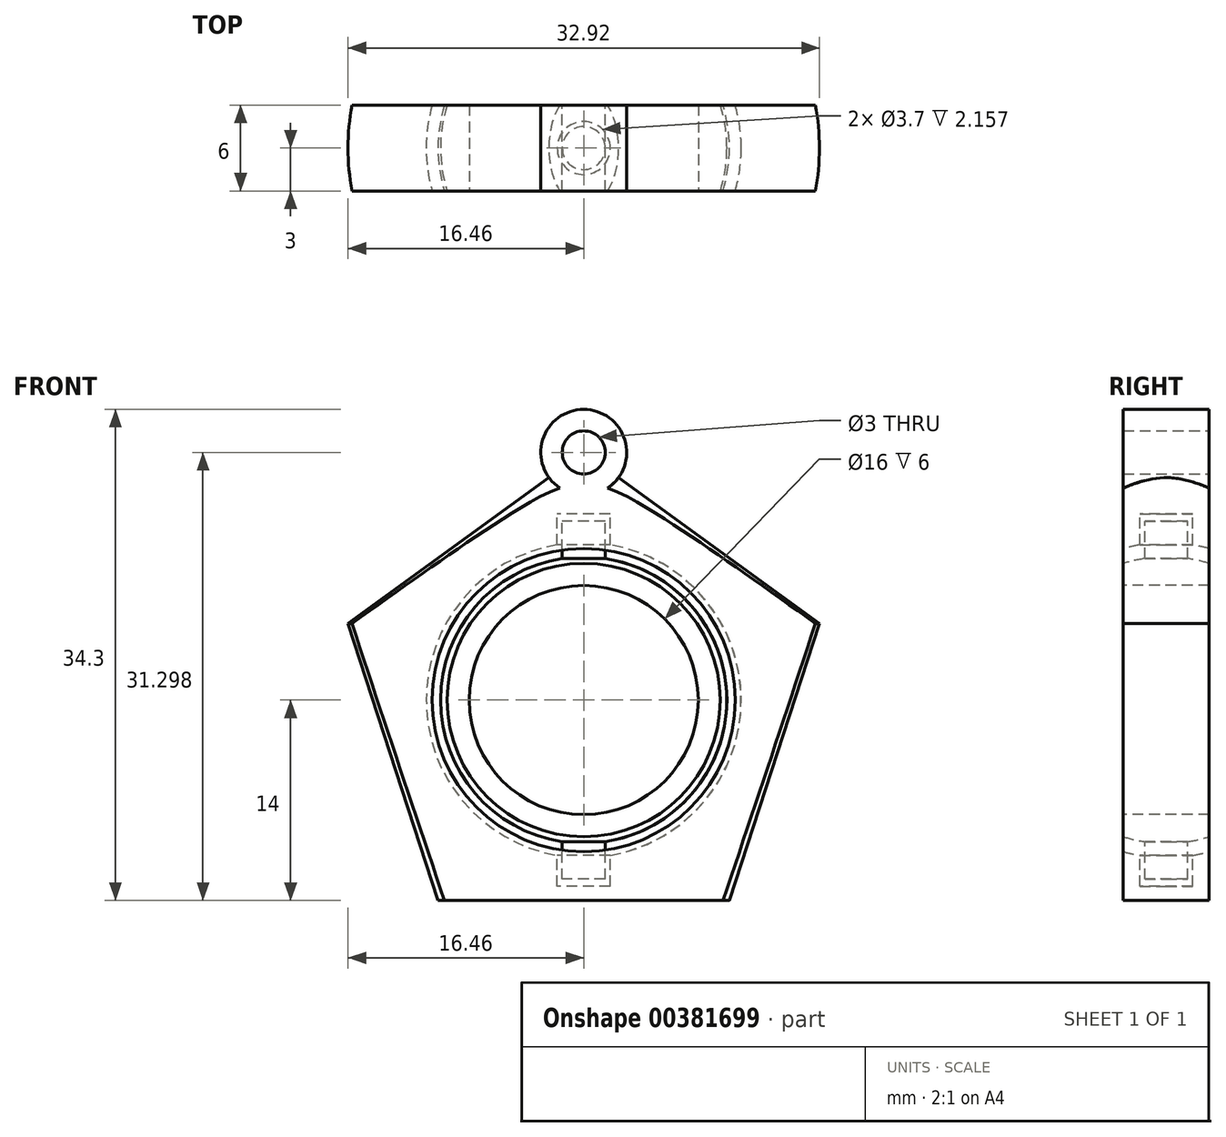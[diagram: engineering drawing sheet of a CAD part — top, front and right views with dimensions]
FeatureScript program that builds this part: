
annotation { "Feature Type Name" : "Feature", "Feature Type Description" : "" }
export const myFeature = defineFeature(function(context is Context, id is Id, definition is map)
    precondition{}
    {
        {
            var Q0;
            Q0=qCreatedBy(makeId("Front.planeOp"),FACE);
            var sketch = newSketch(context, id + "F0", { "sketchPlane" : qUnion([Q0])});
            skLineSegment(sketch, "E0.bottom", {"start": v(1.5, -12.5) * mm, "end": v(-1.5, -12.5) * mm});
            skLineSegment(sketch, "E0.top", {"start": v(1.5, 12.5) * mm, "end": v(-1.5, 12.5) * mm});
            skLineSegment(sketch, "E0.left", {"start": v(1.5, -12.5) * mm, "end": v(1.5, 12.5) * mm});
            skLineSegment(sketch, "E0.right", {"start": v(-1.5, -12.5) * mm, "end": v(-1.5, 12.5) * mm});
            skPoint(sketch, "E0.middle", {"position": v(0, 0) * mm});
            skLineSegment(sketch, "E1.bottom", {"start": v(1.85, -13) * mm, "end": v(-1.85, -13) * mm});
            skLineSegment(sketch, "E1.top", {"start": v(1.85, 13) * mm, "end": v(-1.85, 13) * mm});
            skLineSegment(sketch, "E1.left", {"start": v(1.85, -13) * mm, "end": v(1.85, 13) * mm});
            skLineSegment(sketch, "E1.right", {"start": v(-1.85, -13) * mm, "end": v(-1.85, 13) * mm});
            skCircle(sketch, "E2", {"center": v(0, 0) * mm, "radius": 10 * mm});
            skCircle(sketch, "E3", {"center": v(0, 0) * mm, "radius": 11 * mm});
            skCircle(sketch, "E4.cCircle", {"center": v(0, 0) * mm, "radius": 14 * mm, "construction": true});
            skLineSegment(sketch, "E4.0", {"start": v(10.17, -14) * mm, "end": v(-10.17, -14) * mm});
            skLineSegment(sketch, "E4.1", {"start": v(-10.17, -14) * mm, "end": v(-16.46, 5.35) * mm});
            skLineSegment(sketch, "E4.2", {"start": v(-16.46, 5.35) * mm, "end": v(0, 17.3) * mm});
            skLineSegment(sketch, "E4.3", {"start": v(0, 17.3) * mm, "end": v(16.46, 5.35) * mm});
            skLineSegment(sketch, "E4.4", {"start": v(16.46, 5.35) * mm, "end": v(10.17, -14) * mm});
            skPoint(sketch, "E4.0.midPoint", {"position": v(0, -14) * mm});
            skSolve(sketch);
        }
        {
            var Q0;
            Q0=qCreatedBy(makeId("Front.planeOp"),FACE);
            var sketch = newSketch(context, id + "F1", { "sketchPlane" : qUnion([Q0])});
            skLineSegment(sketch, "E5.0", {"start": v(-16.46, 5.35) * mm, "end": v(0, 17.3) * mm});
            skLineSegment(sketch, "E6.0", {"start": v(0, 17.3) * mm, "end": v(16.46, 5.35) * mm});
            skPoint(sketch, "E7.0", {"position": v(1.85, 13) * mm});
            skLineSegment(sketch, "E8.0", {"start": v(1.5, 12.5) * mm, "end": v(-1.5, 12.5) * mm});
            skPoint(sketch, "E9.0", {"position": v(-1.85, 13) * mm});
            skLineSegment(sketch, "E10.0", {"start": v(1.85, -13) * mm, "end": v(1.85, -10.84) * mm});
            skLineSegment(sketch, "E11.0", {"start": v(1.5, -12.5) * mm, "end": v(1.5, -9.89) * mm});
            skLineSegment(sketch, "E12.0", {"start": v(1.85, 13) * mm, "end": v(-1.85, 13) * mm});
            skLineSegment(sketch, "E13.0", {"start": v(-1.5, -12.5) * mm, "end": v(-1.5, -9.89) * mm});
            skLineSegment(sketch, "E14.0", {"start": v(-1.85, -13) * mm, "end": v(-1.85, -10.84) * mm});
            skArc(sketch, "E15.0", {"start": v(-1.5, 9.89) * mm, "mid": v(-10, 0) * mm, "end": v(-1.5, -9.89) * mm});
            skArc(sketch, "E16.0", {"start": v(-1.85, 10.84) * mm, "mid": v(-11, 0) * mm, "end": v(-1.85, -10.84) * mm});
            skLineSegment(sketch, "E17.0", {"start": v(16.46, 5.35) * mm, "end": v(10.17, -14) * mm});
            skLineSegment(sketch, "E18.0", {"start": v(-10.17, -14) * mm, "end": v(-16.46, 5.35) * mm});
            skLineSegment(sketch, "E19.0", {"start": v(10.17, -14) * mm, "end": v(-10.17, -14) * mm});
            skLineSegment(sketch, "E20.0", {"start": v(1.5, -12.5) * mm, "end": v(-1.5, -12.5) * mm});
            skLineSegment(sketch, "E21.0", {"start": v(1.85, -13) * mm, "end": v(-1.85, -13) * mm});
            skPoint(sketch, "E22.0", {"position": v(0, -14) * mm});
            skLineSegment(sketch, "E23.trimOffspring", {"start": v(1.85, 10.84) * mm, "end": v(1.85, 13) * mm});
            skLineSegment(sketch, "E24.trimOffspring", {"start": v(1.5, 9.89) * mm, "end": v(1.5, 12.5) * mm});
            skLineSegment(sketch, "E25.trimOffspring", {"start": v(-1.5, 9.89) * mm, "end": v(-1.5, 12.5) * mm});
            skLineSegment(sketch, "E26.trimOffspring", {"start": v(-1.85, 10.84) * mm, "end": v(-1.85, 13) * mm});
            skArc(sketch, "E27.trimOffspring", {"start": v(1.5, -9.89) * mm, "mid": v(10, 0) * mm, "end": v(1.5, 9.89) * mm});
            skArc(sketch, "E28.trimOffspring", {"start": v(1.85, -10.84) * mm, "mid": v(11, 0) * mm, "end": v(1.85, 10.84) * mm});
            skSolve(sketch);
        }
        {
            var Q0;
            Q0=qCreatedBy(makeId("Front.planeOp"),FACE);
            var sketch = newSketch(context, id + "F2", { "sketchPlane" : qUnion([Q0])});
            skLineSegment(sketch, "E29.1", {"start": v(0, 17.3) * mm, "end": v(16.46, 5.35) * mm});
            skPoint(sketch, "E29.2", {"position": v(1.85, 13) * mm});
            skLineSegment(sketch, "E29.3", {"start": v(1.5, 12.5) * mm, "end": v(0, 12.5) * mm});
            skPoint(sketch, "E29.4", {"position": v(-1.85, 13) * mm});
            skLineSegment(sketch, "E29.5", {"start": v(1.85, -13) * mm, "end": v(1.85, -10.84) * mm});
            skLineSegment(sketch, "E29.6", {"start": v(1.5, -12.5) * mm, "end": v(1.5, -9.89) * mm});
            skLineSegment(sketch, "E29.7", {"start": v(1.85, 13) * mm, "end": v(0, 13) * mm});
            skLineSegment(sketch, "E29.12", {"start": v(16.46, 5.35) * mm, "end": v(10.17, -14) * mm});
            skLineSegment(sketch, "E29.14", {"start": v(10.17, -14) * mm, "end": v(0, -14) * mm});
            skLineSegment(sketch, "E29.15", {"start": v(1.5, -12.5) * mm, "end": v(0, -12.5) * mm});
            skLineSegment(sketch, "E29.16", {"start": v(1.85, -13) * mm, "end": v(0, -13) * mm});
            skPoint(sketch, "E29.17", {"position": v(0, -14) * mm});
            skLineSegment(sketch, "E29.18", {"start": v(1.85, 10.84) * mm, "end": v(1.85, 13) * mm});
            skLineSegment(sketch, "E29.19", {"start": v(1.5, 9.89) * mm, "end": v(1.5, 12.5) * mm});
            skArc(sketch, "E29.22", {"start": v(1.5, -9.89) * mm, "mid": v(10, 0) * mm, "end": v(1.5, 9.89) * mm});
            skArc(sketch, "E29.23", {"start": v(1.85, -10.84) * mm, "mid": v(11, 0) * mm, "end": v(1.85, 10.84) * mm});
            skLineSegment(sketch, "E30", {"start": v(0, 17.3) * mm, "end": v(0, 13) * mm});
            skPoint(sketch, "E29.0.start.orphan", {"position": v(-16.46, 5.35) * mm});
            skPoint(sketch, "E29.21.end.orphan", {"position": v(-1.85, 13) * mm});
            skPoint(sketch, "E29.21.start.orphan", {"position": v(-1.85, 10.84) * mm});
            skPoint(sketch, "E29.20.end.orphan", {"position": v(-1.5, 12.5) * mm});
            skPoint(sketch, "E29.20.start.orphan", {"position": v(-1.5, 9.89) * mm});
            skPoint(sketch, "E29.11.end.orphan", {"position": v(-1.85, -10.84) * mm});
            skPoint(sketch, "E29.11.start.orphan", {"position": v(-1.85, 10.84) * mm});
            skPoint(sketch, "E29.10.end.orphan", {"position": v(-1.5, -9.89) * mm});
            skPoint(sketch, "E29.10.start.orphan", {"position": v(-1.5, 9.89) * mm});
            skLineSegment(sketch, "E31.trimOffspring", {"start": v(0, 12.5) * mm, "end": v(0, -12.5) * mm});
            skPoint(sketch, "E29.13.end.orphan", {"position": v(-16.46, 5.35) * mm});
            skPoint(sketch, "E29.13.start.orphan", {"position": v(-10.17, -14) * mm});
            skPoint(sketch, "E29.8.end.orphan", {"position": v(-1.5, -9.89) * mm});
            skPoint(sketch, "E29.8.start.orphan", {"position": v(-1.5, -12.5) * mm});
            skPoint(sketch, "E29.9.end.orphan", {"position": v(-1.85, -10.84) * mm});
            skPoint(sketch, "E29.9.start.orphan", {"position": v(-1.85, -13) * mm});
            skLineSegment(sketch, "E32.trimOffspring", {"start": v(0, -13) * mm, "end": v(0, -14) * mm});
            skSolve(sketch);
        }
        {
            var Q0;
            Q0=makeQuery(id+"F2.imprint","IMPRINT",FACE,{"disambiguationData":[TD([[makeQuery(id+"F2.imprint","IMPRINT",EDGE,{"derivedFrom":sQuery(id+"F2.wireOp",EDGE,"E29.3")}),1.0]])]});
            var Q1;
            Q1=makeQuery(id+"F2.imprint","IMPRINT",FACE,{"disambiguationData":[TD([[makeQuery(id+"F2.imprint","IMPRINT",EDGE,{"derivedFrom":sQuery(id+"F2.wireOp",EDGE,"E29.1")}),-1.0]])]});
            var Q2;
            Q2=sQuery(id+"F2.wireOp",EDGE,"E31.trimOffspring");
            revolve(context, id + "F3", {"entities" : qUnion([Q0, Q1]), "axis" : qUnion([Q2]), "revolveType" : RevolveType.FULL});
        }
        {
            var Q0;
            Q0=qCreatedBy(makeId("Right.planeOp"),FACE);
            var sketch = newSketch(context, id + "F4", { "sketchPlane" : qUnion([Q0])});
            skLineSegment(sketch, "E33.bottom", {"start": v(-18.94, 18.05) * mm, "end": v(-3, 18.05) * mm});
            skLineSegment(sketch, "E33.top", {"start": v(-18.94, -18.04) * mm, "end": v(-3, -18.04) * mm});
            skLineSegment(sketch, "E33.left", {"start": v(-18.94, 18.05) * mm, "end": v(-18.94, -18.04) * mm});
            skLineSegment(sketch, "E33.right", {"start": v(-3, 18.05) * mm, "end": v(-3, -18.04) * mm});
            skLineSegment(sketch, "E34.bottom", {"start": v(3, 17.62) * mm, "end": v(19.14, 17.62) * mm});
            skLineSegment(sketch, "E34.top", {"start": v(3, -18.04) * mm, "end": v(19.14, -18.04) * mm});
            skLineSegment(sketch, "E34.left", {"start": v(3, 17.62) * mm, "end": v(3, -18.04) * mm});
            skLineSegment(sketch, "E34.right", {"start": v(19.14, 17.62) * mm, "end": v(19.14, -18.04) * mm});
            skSolve(sketch);
        }
        {
            var Q0;
            Q0 = qSketchRegion(id + "F4", true);
            extrude(context, id + "F5", {"entities" : qUnion([Q0]), "operationType" : NewBodyOperationType.REMOVE, "endBound" : BoundingType.SYMMETRIC, "depth" : 60 * mm});
        }
        {
            var Q0;
            Q0=qCreatedBy(makeId("Front.planeOp"),FACE);
            var sketch = newSketch(context, id + "F6", { "sketchPlane" : qUnion([Q0])});
            skCircle(sketch, "E35", {"center": v(0, 0) * mm, "radius": 8 * mm});
            skCircle(sketch, "E36", {"center": v(0, 17.3) * mm, "radius": 3 * mm});
            skSolve(sketch);
        }
        {
            var Q0;
            Q0 = qSketchRegion(id + "F6", true);
            extrude(context, id + "F7", {"entities" : qUnion([Q0]), "operationType" : NewBodyOperationType.REMOVE, "endBound" : BoundingType.SYMMETRIC, "oppositeDirection" : true, "depth" : 25 * mm});
        }
        {
            var Q0;
            Q0=qCreatedBy(makeId("Front.planeOp"),FACE);
            var sketch = newSketch(context, id + "F8", { "sketchPlane" : qUnion([Q0])});
            skCircle(sketch, "E37.0.0", {"center": v(0, 17.3) * mm, "radius": 3 * mm});
            skCircle(sketch, "E38", {"center": v(0, 17.3) * mm, "radius": 1.5 * mm});
            skSolve(sketch);
        }
        {
            var Q0;
            Q0 = qSketchRegion(id + "F8", true);
            extrude(context, id + "F9", {"entities" : qUnion([Q0]), "operationType" : NewBodyOperationType.ADD, "endBound" : BoundingType.SYMMETRIC, "depth" : 6 * mm});
        }
    });
